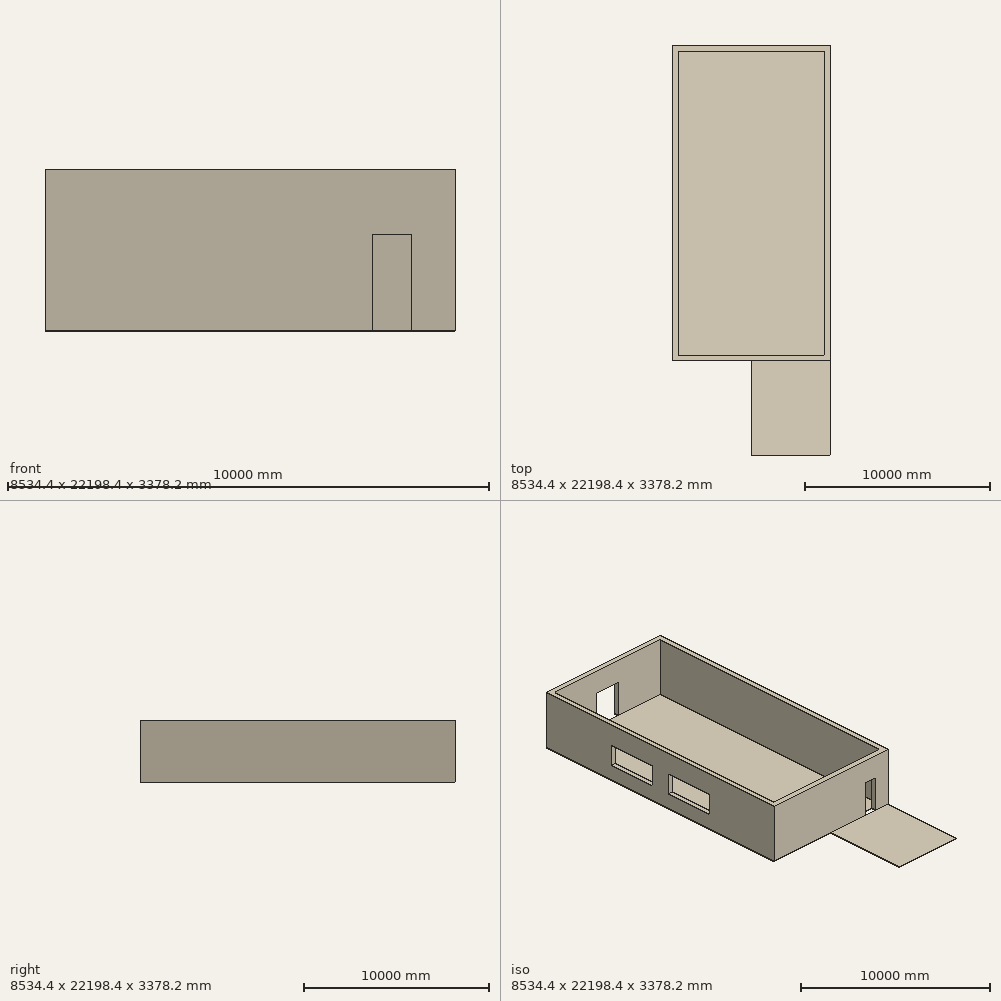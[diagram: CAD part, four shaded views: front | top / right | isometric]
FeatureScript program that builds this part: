
annotation { "Feature Type Name" : "Feature", "Feature Type Description" : "" }
export const myFeature = defineFeature(function(context is Context, id is Id, definition is map)
    precondition{}
    {
        {
            var Q0;
            Q0=qCreatedBy(makeId("Top.planeOp"),FACE);
            var sketch = newSketch(context, id + "F0", { "sketchPlane" : qUnion([Q0])});
            skLineSegment(sketch, "E0.bottom", {"start": v(-3962.4, 8229.6) * mm, "end": v(3962.4, 8229.6) * mm});
            skLineSegment(sketch, "E0.top", {"start": v(-3962.4, -8229.6) * mm, "end": v(3962.4, -8229.6) * mm});
            skLineSegment(sketch, "E0.left", {"start": v(-3962.4, 8229.6) * mm, "end": v(-3962.4, -8229.6) * mm});
            skLineSegment(sketch, "E0.right", {"start": v(3962.4, 8229.6) * mm, "end": v(3962.4, -8229.6) * mm});
            skPoint(sketch, "E0.middle", {"position": v(0, 0) * mm});
            skLineSegment(sketch, "E1.0", {"start": v(-4267.2, 8534.4) * mm, "end": v(-4267.2, -8534.4) * mm});
            skLineSegment(sketch, "E1.1", {"start": v(-4267.2, 8534.4) * mm, "end": v(4267.2, 8534.4) * mm});
            skLineSegment(sketch, "E1.2", {"start": v(4267.2, 8534.4) * mm, "end": v(4267.2, -8534.4) * mm});
            skLineSegment(sketch, "E1.3", {"start": v(-4267.2, -8534.4) * mm, "end": v(4267.2, -8534.4) * mm});
            skSolve(sketch);
        }
        {
            var Q0;
            Q0 = qSketchRegion(id + "F0", true);
            extrude(context, id + "F1", {"entities" : qUnion([Q0]), "depth" : 3352.8 * mm});
        }
        {
            var Q0;
            Q0=makeQuery(id+"F1.opExtrude","CAP_FACE",FACE,{"disambiguationData":[OSD([sQuery(id+"F0.wireOp",EDGE,"E0.bottom"),sQuery(id+"F0.wireOp",EDGE,"E0.top"),sQuery(id+"F0.wireOp",EDGE,"E0.left"),sQuery(id+"F0.wireOp",EDGE,"E0.right"),sQuery(id+"F0.wireOp",EDGE,"E1.0"),sQuery(id+"F0.wireOp",EDGE,"E1.1"),sQuery(id+"F0.wireOp",EDGE,"E1.2"),sQuery(id+"F0.wireOp",EDGE,"E1.3")])],"isStart":true});
            var sketch = newSketch(context, id + "F2", { "sketchPlane" : qUnion([Q0])});
            skLineSegment(sketch, "E2.bottom", {"start": v(-4267.2, 8534.4) * mm, "end": v(0, 8534.4) * mm});
            skLineSegment(sketch, "E2.top", {"start": v(-4267.2, -8534.4) * mm, "end": v(4267.2, -8534.4) * mm});
            skLineSegment(sketch, "E2.left", {"start": v(-4267.2, 8534.4) * mm, "end": v(-4267.2, -8534.4) * mm});
            skLineSegment(sketch, "E2.right", {"start": v(4267.2, 8534.4) * mm, "end": v(4267.2, -8534.4) * mm});
            skLineSegment(sketch, "E3", {"start": v(4267.2, 8534.4) * mm, "end": v(4267.2, 13663.98) * mm});
            skLineSegment(sketch, "E4", {"start": v(4267.2, 13663.98) * mm, "end": v(0, 13663.98) * mm});
            skLineSegment(sketch, "E5", {"start": v(0, 13663.98) * mm, "end": v(0, 8534.4) * mm});
            skSolve(sketch);
        }
        {
            var Q0;
            Q0 = qSketchRegion(id + "F2", true);
            extrude(context, id + "F3", {"entities" : qUnion([Q0]), "depth" : 25.4 * mm});
        }
        {
            var Q0;
            Q0=makeQuery(id+"F3.boolean.opBoolean","MERGE",FACE,{"derivedFrom":[makeQuery(id+"F1.opExtrude","SWEPT_FACE",FACE,{"disambiguationData":[OSD([sQuery(id+"F0.wireOp",EDGE,"E1.3")])]}),makeQuery(id+"F3.opExtrude","SWEPT_FACE",FACE,{"disambiguationData":[OSD([sQuery(id+"F2.wireOp",EDGE,"E2.bottom")])]})]});
            var sketch = newSketch(context, id + "F4", { "sketchPlane" : qUnion([Q0])});
            skLineSegment(sketch, "E6.bottom", {"start": v(3352.8, -25.4) * mm, "end": v(2540, -25.4) * mm});
            skLineSegment(sketch, "E6.top", {"start": v(3352.8, 2006.6) * mm, "end": v(2540, 2006.6) * mm});
            skLineSegment(sketch, "E6.left", {"start": v(3352.8, -25.4) * mm, "end": v(3352.8, 2006.6) * mm});
            skLineSegment(sketch, "E6.right", {"start": v(2540, -25.4) * mm, "end": v(2540, 2006.6) * mm});
            skSolve(sketch);
        }
        {
            var Q0;
            Q0 = qSketchRegion(id + "F4", true);
            var Q1;
            Q1=makeQuery(id+"F1.opExtrude","SWEPT_FACE",FACE,{"disambiguationData":[OSD([sQuery(id+"F0.wireOp",EDGE,"E0.top")])]});
            extrude(context, id + "F5", {"entities" : qUnion([Q0]), "operationType" : NewBodyOperationType.REMOVE, "endBound" : BoundingType.UP_TO_SURFACE, "oppositeDirection" : true, "endBoundEntityFace" : qUnion([Q1]), "depth" : 25.4 * mm});
        }
        {
            var Q0;
            Q0=makeQuery(id+"F3.boolean.opBoolean","MERGE",FACE,{"derivedFrom":[makeQuery(id+"F1.opExtrude","SWEPT_FACE",FACE,{"disambiguationData":[OSD([sQuery(id+"F0.wireOp",EDGE,"E1.0")])]}),makeQuery(id+"F3.opExtrude","SWEPT_FACE",FACE,{"disambiguationData":[OSD([sQuery(id+"F2.wireOp",EDGE,"E2.left")])]})]});
            var sketch = newSketch(context, id + "F6", { "sketchPlane" : qUnion([Q0])});
            skLineSegment(sketch, "E7", {"start": v(0, 3352.8) * mm, "end": v(0, 0) * mm, "construction": true});
            skLineSegment(sketch, "E8.bottom", {"start": v(-3657.6, 2108.2) * mm, "end": v(-609.6, 2108.2) * mm});
            skLineSegment(sketch, "E8.top", {"start": v(-3657.6, 889) * mm, "end": v(-609.6, 889) * mm});
            skLineSegment(sketch, "E8.left", {"start": v(-3657.6, 2108.2) * mm, "end": v(-3657.6, 889) * mm});
            skLineSegment(sketch, "E8.right", {"start": v(-609.6, 2108.2) * mm, "end": v(-609.6, 889) * mm});
            skLineSegment(sketch, "E9.MirrorCS", {"start": v(609.6, 2108.2) * mm, "end": v(609.6, 889) * mm});
            skLineSegment(sketch, "E10.MirrorCS", {"start": v(3657.6, 2108.2) * mm, "end": v(3657.6, 889) * mm});
            skLineSegment(sketch, "E11.MirrorCS", {"start": v(3657.6, 889) * mm, "end": v(609.6, 889) * mm});
            skLineSegment(sketch, "E12.MirrorCS", {"start": v(3657.6, 2108.2) * mm, "end": v(609.6, 2108.2) * mm});
            skSolve(sketch);
        }
        {
            var Q0;
            Q0 = qSketchRegion(id + "F6", true);
            var Q1;
            Q1=makeQuery(id+"F1.opExtrude","SWEPT_FACE",FACE,{"disambiguationData":[OSD([sQuery(id+"F0.wireOp",EDGE,"E0.left")])]});
            extrude(context, id + "F7", {"entities" : qUnion([Q0]), "operationType" : NewBodyOperationType.REMOVE, "endBound" : BoundingType.UP_TO_SURFACE, "oppositeDirection" : true, "endBoundEntityFace" : qUnion([Q1]), "depth" : 25.4 * mm});
        }
        {
            var Q0;
            Q0=makeQuery(id+"F3.boolean.opBoolean","MERGE",FACE,{"derivedFrom":[makeQuery(id+"F1.opExtrude","SWEPT_FACE",FACE,{"disambiguationData":[OSD([sQuery(id+"F0.wireOp",EDGE,"E1.1")])]}),makeQuery(id+"F3.opExtrude","SWEPT_FACE",FACE,{"disambiguationData":[OSD([sQuery(id+"F2.wireOp",EDGE,"E2.top")])]})]});
            var sketch = newSketch(context, id + "F8", { "sketchPlane" : qUnion([Q0])});
            skLineSegment(sketch, "E13", {"start": v(0, -25.4) * mm, "end": v(0, 3352.8) * mm, "construction": true});
            skLineSegment(sketch, "E14", {"start": v(0, 2006.6) * mm, "end": v(-812.8, 2006.6) * mm});
            skLineSegment(sketch, "E15", {"start": v(-812.8, 2006.6) * mm, "end": v(-812.8, -25.4) * mm});
            skLineSegment(sketch, "E16.MirrorCS", {"start": v(0, 2006.6) * mm, "end": v(812.8, 2006.6) * mm});
            skLineSegment(sketch, "E17.MirrorCS", {"start": v(812.8, 2006.6) * mm, "end": v(812.8, -25.4) * mm});
            skLineSegment(sketch, "E18", {"start": v(-812.8, -25.4) * mm, "end": v(0, -25.4) * mm});
            skLineSegment(sketch, "E19.MirrorCS", {"start": v(812.8, -25.4) * mm, "end": v(0, -25.4) * mm});
            skSolve(sketch);
        }
        {
            var Q0;
            Q0 = qSketchRegion(id + "F8", true);
            var Q1;
            Q1=makeQuery(id+"F1.opExtrude","SWEPT_FACE",FACE,{"disambiguationData":[OSD([sQuery(id+"F0.wireOp",EDGE,"E0.bottom")])]});
            extrude(context, id + "F9", {"entities" : qUnion([Q0]), "operationType" : NewBodyOperationType.REMOVE, "endBound" : BoundingType.UP_TO_SURFACE, "oppositeDirection" : true, "endBoundEntityFace" : qUnion([Q1]), "depth" : 25.4 * mm});
        }
    });
